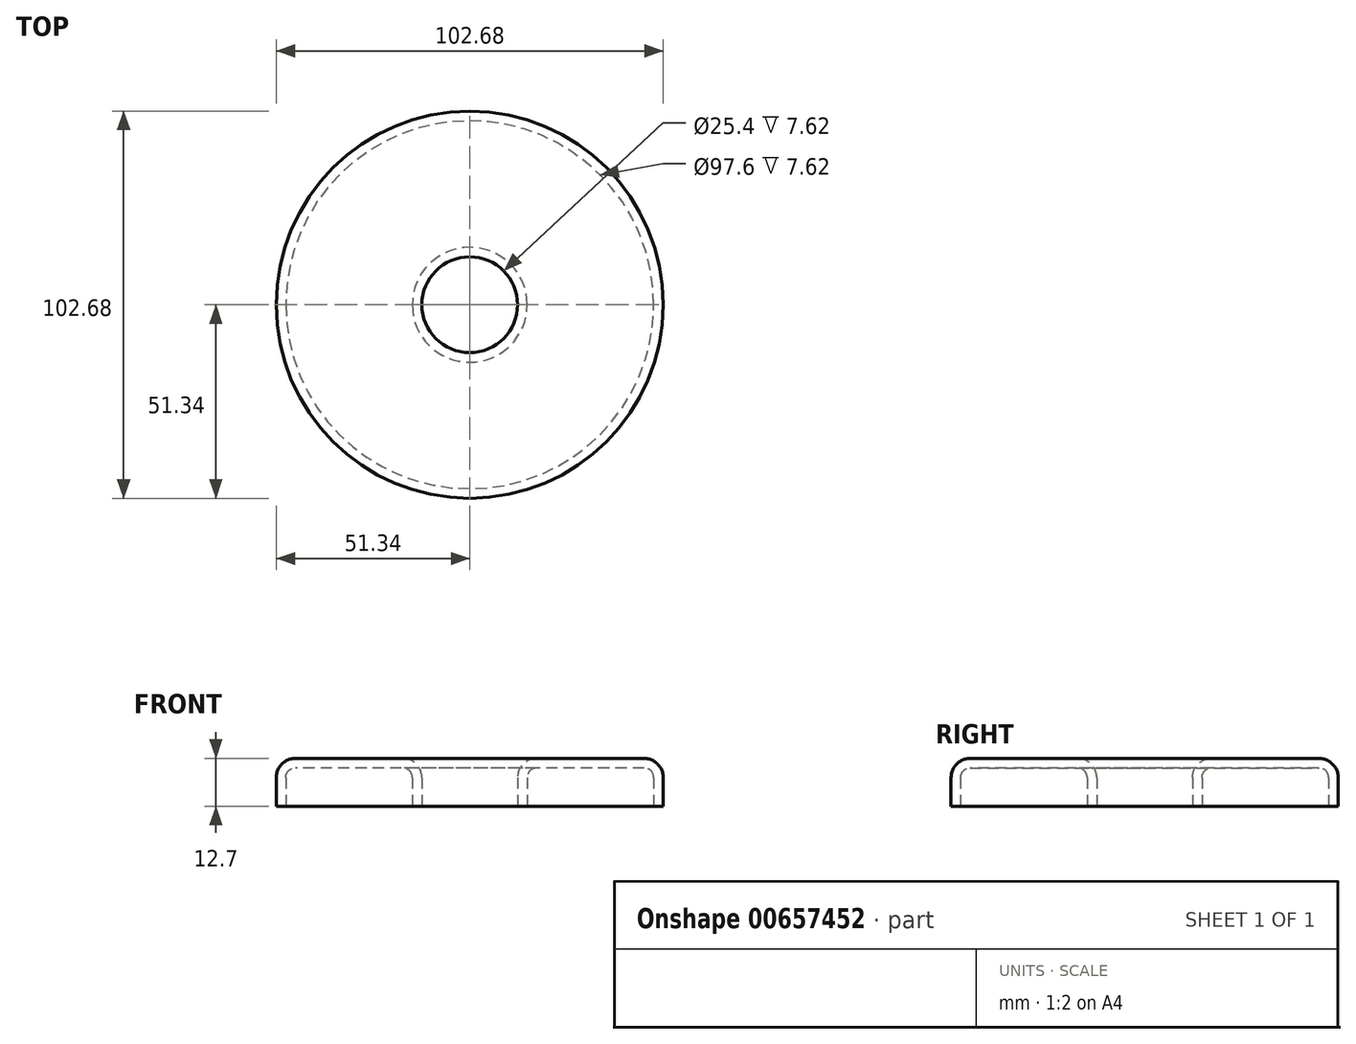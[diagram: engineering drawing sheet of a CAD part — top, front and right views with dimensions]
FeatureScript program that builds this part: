
annotation { "Feature Type Name" : "Feature", "Feature Type Description" : "" }
export const myFeature = defineFeature(function(context is Context, id is Id, definition is map)
    precondition{}
    {
        {
            var Q0;
            Q0=qCreatedBy(makeId("Top.planeOp"),FACE);
            var sketch = newSketch(context, id + "F0", { "sketchPlane" : qUnion([Q0])});
            skCircle(sketch, "E0", {"center": v(0, 0) * mm, "radius": 51.34 * mm});
            skCircle(sketch, "E1", {"center": v(0, 0) * mm, "radius": 12.7 * mm});
            skSolve(sketch);
        }
        {
            var Q0;
            Q0=makeQuery(id+"F0.imprint","IMPRINT",FACE,{"disambiguationData":[TD([[makeQuery(id+"F0.imprint","IMPRINT",EDGE,{"derivedFrom":sQuery(id+"F0.wireOp",EDGE,"E0")}),1.0]])]});
            extrude(context, id + "F1", {"entities" : qUnion([Q0]), "depth" : 12.7 * mm, "offsetDistance" : 25.4 * mm});
        }
        {
            var Q0;
            Q0=makeQuery(id+"F1.opExtrude","CAP_FACE",FACE,{"disambiguationData":[OSD([sQuery(id+"F0.wireOp",EDGE,"E0"),sQuery(id+"F0.wireOp",EDGE,"E1")])],"isStart":false});
            fillet(context, id + "F2", {"entities" : qUnion([Q0]), "radius" : 5.08 * mm, "tangentPropagation" : true, "allowEdgeOverflow" : false});
        }
        {
            var Q0;
            Q0=makeQuery(id+"F1.opExtrude","CAP_FACE",FACE,{"disambiguationData":[OSD([sQuery(id+"F0.wireOp",EDGE,"E0"),sQuery(id+"F0.wireOp",EDGE,"E1")])],"isStart":true});
            shell(context, id + "F3", {"entities" : qUnion([Q0]), "thickness" : 2.54 * mm});
        }
    });
